# Revit family: DockShelter_BlueGiant_BG450IS
name_source: partatom
category: Specialty Equipment
units: mm (PartAtom-declared; Revit-internal decimal feet)

## family parameters
Always vertical = Yes
Cut with Voids When Loaded = No
Enable Cutting in Views = No
Maintain Annotation Orientation = No
Part Type = Normal
Room Calculation Point = No
Round Connector Dimension = Use Diameter
Shared = No
Work Plane-Based = Yes

## types (1)
- Standard Unit
    Assembly Code = E1030300
    Construction Details = http://www.arcat.com
    Default Elevation = 4' - 0"
    Description = As Specified in 11160
    Door Opening Height = 10' - 0"
    Door Opening Width = 10' - 0"
    Expected Lifespan (Years) = 0
    Fabric Color = Fabric - Blue Giant - 22oz HT Blue Vinyl
    Green Building-LEED = http://www.arcat.com
    Installation_Fabricaton = http://www.bluegiant.com
    Keynote = 11160
    Maintenance Schedule (Months) = 0
    Manufacturer = Blue Giant Equipment Corp.
    Manufacturer Fax = 905-457-2313
    Manufacturer Website = http://www.bluegiant.com
    Model = As Specified in 11160
    Product Data = http://www.arcat.com
    Product Properties = http://www.arcat.com
    Projection = 3' - 0"
    Sales Information = http://www.bluegiant.com
    Send Message = http://admin.arcat.com
    SpecWizard = http://www.arcat.com
    Specification = http://www.arcat.com
    Truck Guide Color = Fabric - Blue Giant - Yellow Guide
    URL = http://www.bluegiant.com
    Warranty Duration (Years) = 0

## geometry (parser evidence)
native form markers: Sweep x2
no freeform markers — native parametric forms only
